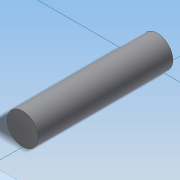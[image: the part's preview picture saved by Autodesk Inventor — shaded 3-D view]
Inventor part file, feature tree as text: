
AUTODESK INVENTOR PART (.ipt)
format: ipt  version: 2014 SP2 (Build 180246200, 246)  size: 81,408 bytes
history: native  units: in
note: dims shown in document units (in); Inventor stores cm internally (conversion verified against a paired STEP export)
features: extrude x2, sketch x2
ambient origin geometry x8: Origin, YZ Plane, XZ Plane, XY Plane, X Axis, Y Axis, Z Axis, Center Point
bodies: Solid1 (feature_tree)
feature tree (4):
  extrude  "Extrusion1"  Depth=0.8105in TaperAngle=0.0deg
  extrude  "Extrusion2"  Depth=0.559in TaperAngle=0.0deg
  sketch  "Sketch1"  dims[d0=0.1875in d1=0.8105in d2=0.0in]
  sketch  "Sketch2"  dims[d3=0.157in d4=0.559in d5=0.0in]
